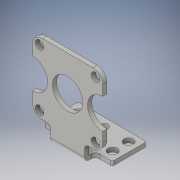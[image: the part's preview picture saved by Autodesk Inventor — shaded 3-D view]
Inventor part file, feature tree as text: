
AUTODESK INVENTOR PART (.ipt)
format: ipt  version: 2016 (Build 200138000, 138)  size: 249,856 bytes
history: native  units: in
note: dims shown in document units (in); Inventor stores cm internally (conversion verified against a paired STEP export)
features: extrude x7, sketch x7, fillet x5
ambient origin geometry x8: Origin, YZ Plane, XZ Plane, XY Plane, X Axis, Y Axis, Z Axis, Center Point
bodies: Solid1 (feature_tree)
feature tree (19):
  extrude  "Extrusion1"  Depth=0.89in
  fillet  "Fillet1"  Radius=0.384in
  extrude  "Extrusion2"  Depth=0.055in TaperAngle=0.0deg
  extrude  "Extrusion3"  Depth=0.055in
  fillet  "Fillet2"  Radius=0.055in
  extrude  "Extrusion4"  Depth=0.2165in
  extrude  "Extrusion5"  Depth=0.05in
  fillet  "Fillet3"  Radius=0.055in
  fillet  "Fillet4"  Radius=0.05in
  extrude  "Extrusion8"  Depth=0.055in TaperAngle=0.0deg
  fillet  "Fillet5"  Radius=0.868in
  extrude  "Extrusion10"  Depth=0.05in
  sketch  "Sketch1"  dims[d2=0.89in d3=0.89in d4=0.384in]
  sketch  "Sketch2"  dims[d5=0.384in d6=0.055in d7=0.0in]
  sketch  "Sketch3"  dims[d8=0.125in d9=0.11in d10=0.055in d11=0.0in]
  sketch  "Sketch4"  dims[d12=0.2165in d13=0.2165in]
  sketch  "Sketch5"  dims[d14=0.075in d16=0.075in d17=0.055in d18=0.0in d19=0.05in]
  sketch  "Sketch8"  dims[d20=0.081in d21=0.055in d22=0.0in d25=0.868in]
  sketch  "Sketch11"  dims[d26=0.055in d27=0.0in d28=0.05in d29=0.02in d35=0.055in d36=0.0in d37=0.06in d38=0.433in d43=0.119in d47=0.113in d50=0.104in d51=0.077in d52=1.0in d53=0.0in]
